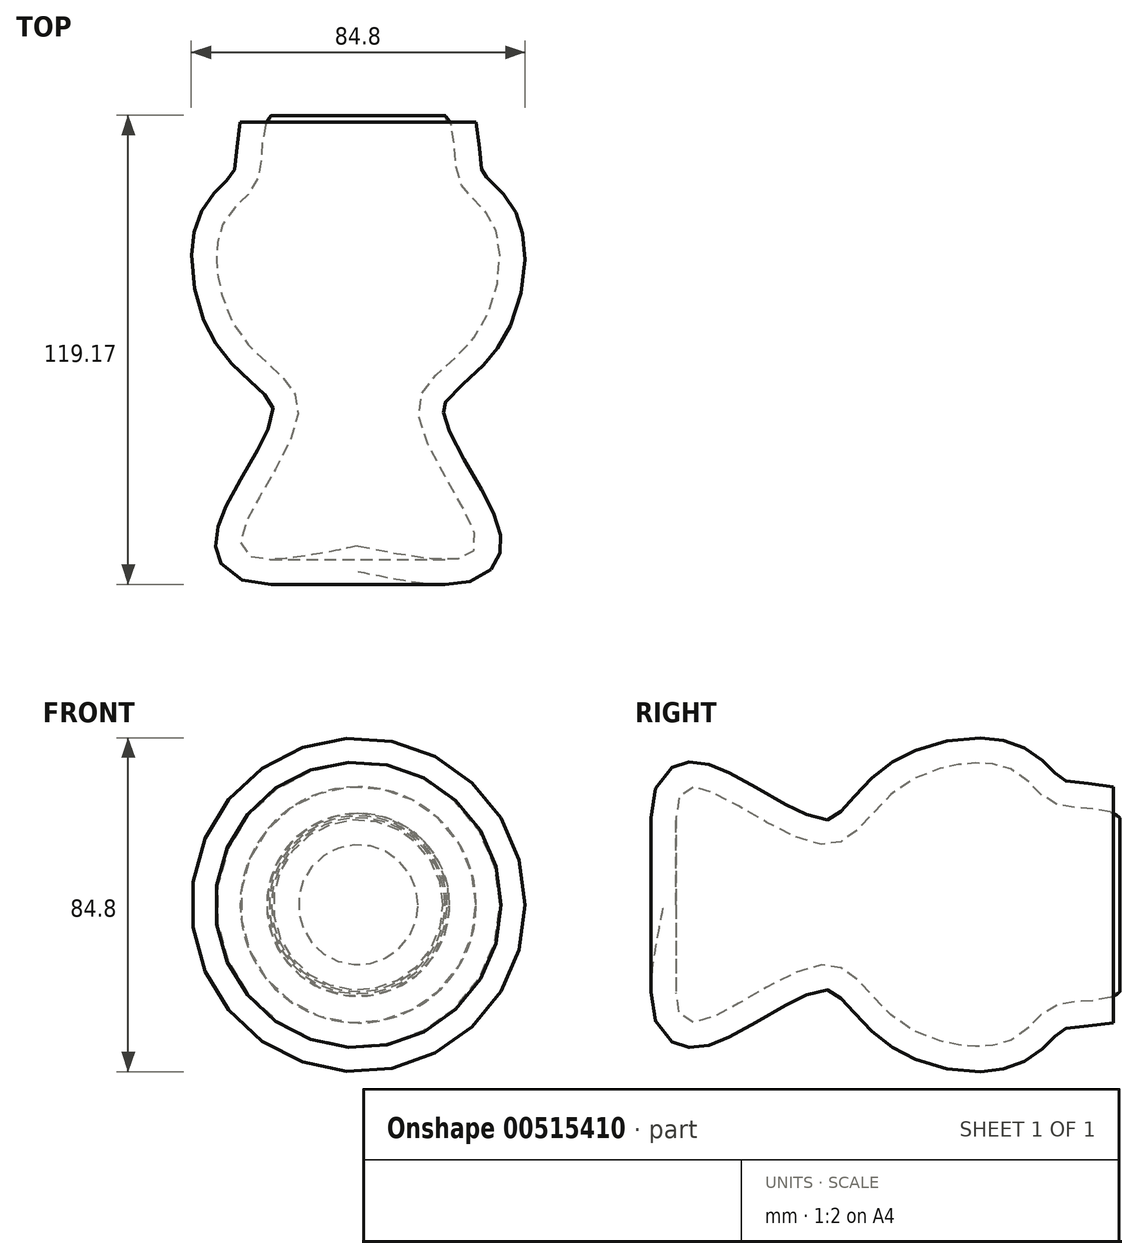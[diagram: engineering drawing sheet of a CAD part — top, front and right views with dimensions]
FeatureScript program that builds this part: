
annotation { "Feature Type Name" : "Feature", "Feature Type Description" : "" }
export const myFeature = defineFeature(function(context is Context, id is Id, definition is map)
    precondition{}
    {
        {
            var Q0;
            Q0=qCreatedBy(makeId("Top.planeOp"),FACE);
            var sketch = newSketch(context, id + "F0", { "sketchPlane" : qUnion([Q0])});
            skLineSegment(sketch, "E0", {"start": v(0, 75.74) * mm, "end": v(0, -76.35) * mm});
            skFitSpline(sketch, "E1", {"points": [v(0, -56.24) * mm, v(29.87, -56.24) * mm, v(15.24, -22.1) * mm, v(29.57, -3.2) * mm, v(34.44, 25.45) * mm, v(25.6, 36.73) * mm, v(22.56, 52.58) * mm, v(0, 53.8) * mm], "startDerivative": vector(271.63, -55.37) * mm, "endDerivative": vector(-208.33, -32.23) * mm});
            skFitSpline(sketch, "E2.0", {"points": [v(-1.27, -62.46) * mm, v(0.15, -62.75) * mm, v(3, -63.33) * mm, v(7.24, -64.16) * mm, v(11.39, -64.9) * mm, v(15.4, -65.5) * mm, v(19.22, -65.9) * mm, v(22.24, -66) * mm, v(24.58, -65.92) * mm, v(26.33, -65.73) * mm, v(28.08, -65.39) * mm, v(29.87, -64.82) * mm, v(31.7, -63.91) * mm, v(33.2, -62.76) * mm, v(34.28, -61.56) * mm, v(34.98, -60.53) * mm, v(35.54, -59.4) * mm, v(35.88, -58.42) * mm, v(36.07, -57.62) * mm, v(36.22, -56.83) * mm, v(36.3, -55.89) * mm, v(36.29, -54.82) * mm, v(36.16, -53.49) * mm, v(35.85, -51.95) * mm, v(35.32, -50.23) * mm, v(34.68, -48.55) * mm, v(33.94, -46.9) * mm, v(33.12, -45.24) * mm, v(31.95, -43.02) * mm, v(30.36, -40.2) * mm, v(28.37, -36.8) * mm, v(26.42, -33.4) * mm, v(24.64, -30.14) * mm, v(23.4, -27.6) * mm, v(22.63, -25.75) * mm, v(22.16, -24.49) * mm, v(21.84, -23.38) * mm, v(21.67, -22.61) * mm, v(21.6, -22.11) * mm, v(21.58, -21.8) * mm, v(21.58, -21.56) * mm, v(21.59, -21.26) * mm, v(21.64, -20.95) * mm, v(21.74, -20.59) * mm, v(21.9, -20.2) * mm, v(22.24, -19.57) * mm, v(22.96, -18.6) * mm, v(24.36, -17.15) * mm, v(26.22, -15.48) * mm, v(28.4, -13.58) * mm, v(30.4, -11.76) * mm, v(32.03, -10.11) * mm, v(33.25, -8.77) * mm, v(34.25, -7.55) * mm, v(35.02, -6.5) * mm, v(35.76, -5.45) * mm, v(36.62, -4.09) * mm, v(37.88, -1.84) * mm, v(39.22, 1.07) * mm, v(40.5, 4.67) * mm, v(41.45, 8.33) * mm, v(42.08, 12.01) * mm, v(42.38, 15.66) * mm, v(42.35, 18.65) * mm, v(42.14, 20.99) * mm, v(41.88, 22.72) * mm, v(41.52, 24.42) * mm, v(41.03, 26.08) * mm, v(40.52, 27.44) * mm, v(40.03, 28.5) * mm, v(39.5, 29.52) * mm, v(38.8, 30.69) * mm, v(37.6, 32.36) * mm, v(36.06, 34.09) * mm, v(34.39, 35.7) * mm, v(33.27, 36.77) * mm, v(32.6, 37.48) * mm, v(32.2, 37.95) * mm, v(31.9, 38.34) * mm, v(31.72, 38.61) * mm, v(31.62, 38.81) * mm, v(31.56, 38.93) * mm, v(31.53, 39.02) * mm, v(31.5, 39.1) * mm, v(31.44, 39.26) * mm, v(31.37, 39.49) * mm, v(31.28, 39.85) * mm, v(31.13, 40.65) * mm, v(30.97, 42.18) * mm, v(30.85, 44.42) * mm, v(30.7, 46.95) * mm, v(30.46, 49.26) * mm, v(30.05, 51.24) * mm, v(29.6, 52.8) * mm, v(29.03, 54.15) * mm, v(28.43, 55.24) * mm, v(27.9, 56.06) * mm, v(27.27, 56.87) * mm, v(26.58, 57.6) * mm, v(25.84, 58.26) * mm, v(24.82, 59.04) * mm, v(23.48, 59.82) * mm, v(21.86, 60.51) * mm, v(20.24, 61) * mm, v(18.1, 61.44) * mm, v(15.42, 61.69) * mm, v(12.2, 61.67) * mm, v(8.94, 61.43) * mm, v(5.63, 61.05) * mm, v(2.3, 60.58) * mm, v(0.11, 60.24) * mm, v(-0.97, 60.07) * mm]});
            skFitSpline(sketch, "E3.trimOffspring", {"points": [v(-1.27, -62.46) * mm, v(0.15, -62.75) * mm, v(3, -63.33) * mm, v(7.24, -64.16) * mm, v(11.39, -64.9) * mm, v(15.4, -65.5) * mm, v(19.22, -65.9) * mm, v(22.24, -66) * mm, v(24.58, -65.92) * mm, v(26.33, -65.73) * mm, v(28.08, -65.39) * mm, v(29.87, -64.82) * mm, v(31.7, -63.91) * mm, v(33.2, -62.76) * mm, v(34.28, -61.56) * mm, v(34.98, -60.53) * mm, v(35.54, -59.4) * mm, v(35.88, -58.42) * mm, v(36.07, -57.62) * mm, v(36.22, -56.83) * mm, v(36.3, -55.89) * mm, v(36.29, -54.82) * mm, v(36.16, -53.49) * mm, v(35.85, -51.95) * mm, v(35.32, -50.23) * mm, v(34.68, -48.55) * mm, v(33.94, -46.9) * mm, v(33.12, -45.24) * mm, v(31.95, -43.02) * mm, v(30.36, -40.2) * mm, v(28.37, -36.8) * mm, v(26.42, -33.4) * mm, v(24.64, -30.14) * mm, v(23.4, -27.6) * mm, v(22.63, -25.75) * mm, v(22.16, -24.49) * mm, v(21.84, -23.38) * mm, v(21.67, -22.61) * mm, v(21.6, -22.11) * mm, v(21.58, -21.8) * mm, v(21.58, -21.56) * mm, v(21.59, -21.26) * mm, v(21.64, -20.95) * mm, v(21.74, -20.59) * mm, v(21.9, -20.2) * mm, v(22.24, -19.57) * mm, v(22.96, -18.6) * mm, v(24.36, -17.15) * mm, v(26.22, -15.48) * mm, v(28.4, -13.58) * mm, v(30.4, -11.76) * mm, v(32.03, -10.11) * mm, v(33.25, -8.77) * mm, v(34.25, -7.55) * mm, v(35.02, -6.5) * mm, v(35.76, -5.45) * mm, v(36.62, -4.09) * mm, v(37.88, -1.84) * mm, v(39.22, 1.07) * mm, v(40.5, 4.67) * mm, v(41.45, 8.33) * mm, v(42.08, 12.01) * mm, v(42.38, 15.66) * mm, v(42.35, 18.65) * mm, v(42.14, 20.99) * mm, v(41.88, 22.72) * mm, v(41.52, 24.42) * mm, v(41.03, 26.08) * mm, v(40.52, 27.44) * mm, v(40.03, 28.5) * mm, v(39.5, 29.52) * mm, v(38.8, 30.69) * mm, v(37.6, 32.36) * mm, v(36.06, 34.09) * mm, v(34.39, 35.7) * mm, v(33.27, 36.77) * mm, v(32.6, 37.48) * mm, v(32.2, 37.95) * mm, v(31.9, 38.34) * mm, v(31.72, 38.61) * mm, v(31.62, 38.81) * mm, v(31.56, 38.93) * mm, v(31.53, 39.02) * mm, v(31.5, 39.1) * mm, v(31.44, 39.26) * mm, v(31.37, 39.49) * mm, v(31.28, 39.85) * mm, v(31.13, 40.65) * mm, v(30.97, 42.18) * mm, v(30.85, 44.42) * mm, v(30.7, 46.95) * mm, v(30.46, 49.26) * mm, v(30.05, 51.24) * mm, v(29.6, 52.8) * mm, v(29.03, 54.15) * mm, v(28.43, 55.24) * mm, v(27.9, 56.06) * mm, v(27.27, 56.87) * mm, v(26.58, 57.6) * mm, v(25.84, 58.26) * mm, v(24.82, 59.04) * mm, v(23.48, 59.82) * mm, v(21.86, 60.51) * mm, v(20.24, 61) * mm, v(18.1, 61.44) * mm, v(15.42, 61.69) * mm, v(12.2, 61.67) * mm, v(8.94, 61.43) * mm, v(5.63, 61.05) * mm, v(2.3, 60.58) * mm, v(0.11, 60.24) * mm, v(-0.97, 60.07) * mm]});
            skLineSegment(sketch, "E4", {"start": v(23.56, 50.72) * mm, "end": v(30.15, 50.72) * mm});
            skFitSpline(sketch, "E5", {"points": [v(0, 60.22) * mm, v(7.72, 60.22) * mm, v(20.18, 55.68) * mm, v(22.56, 51.5) * mm], "startDerivative": vector(21.13, 2.13) * mm, "endDerivative": vector(4.85, -16.96) * mm});
            skFitSpline(sketch, "E6", {"points": [v(22.56, 51.5) * mm, v(30.8, 51.5) * mm], "startDerivative": vector(8.24, 0) * mm, "endDerivative": vector(8.24, 0) * mm});
            skFitSpline(sketch, "E7", {"points": [v(30.8, 51.5) * mm, v(31.43, 48.77) * mm, v(32.24, 48.7) * mm, v(31.68, 53.43) * mm, v(25.08, 54.64) * mm, v(21.3, 58.66) * mm, v(3.46, 64.5) * mm, v(3.46, 65.9) * mm, v(8.24, 67.17) * mm, v(5.43, 69.7) * mm, v(-0.97, 70.97) * mm], "startDerivative": vector(4.12, -43.86) * mm, "endDerivative": vector(-55.04, 3.97) * mm});
            skSolve(sketch);
        }
        {
            var Q0;
            {var subQ0=sQuery(id+"F0.wireOp",EDGE,"E5");Q0=makeQuery(id+"F0.imprint","IMPRINT",FACE,{"disambiguationData":[TD([[makeQuery(id+"F0.imprint","IMPRINT",EDGE,{"derivedFrom":subQ0}),1.0]])]});}
            var Q1;
            {var subQ0=sQuery(id+"F0.wireOp",EDGE,"E1");Q1=makeQuery(id+"F0.imprint","IMPRINT",FACE,{"disambiguationData":[TD([[makeQuery(id+"F0.imprint","IMPRINT",EDGE,{"derivedFrom":subQ0}),-1.0]])]});}
            var Q2;
            Q2=sQuery(id+"F0.wireOp",EDGE,"E0");
            revolve(context, id + "F1", {"entities" : qUnion([Q0, Q1]), "axis" : qUnion([Q2]), "revolveType" : RevolveType.FULL});
        }
    });
